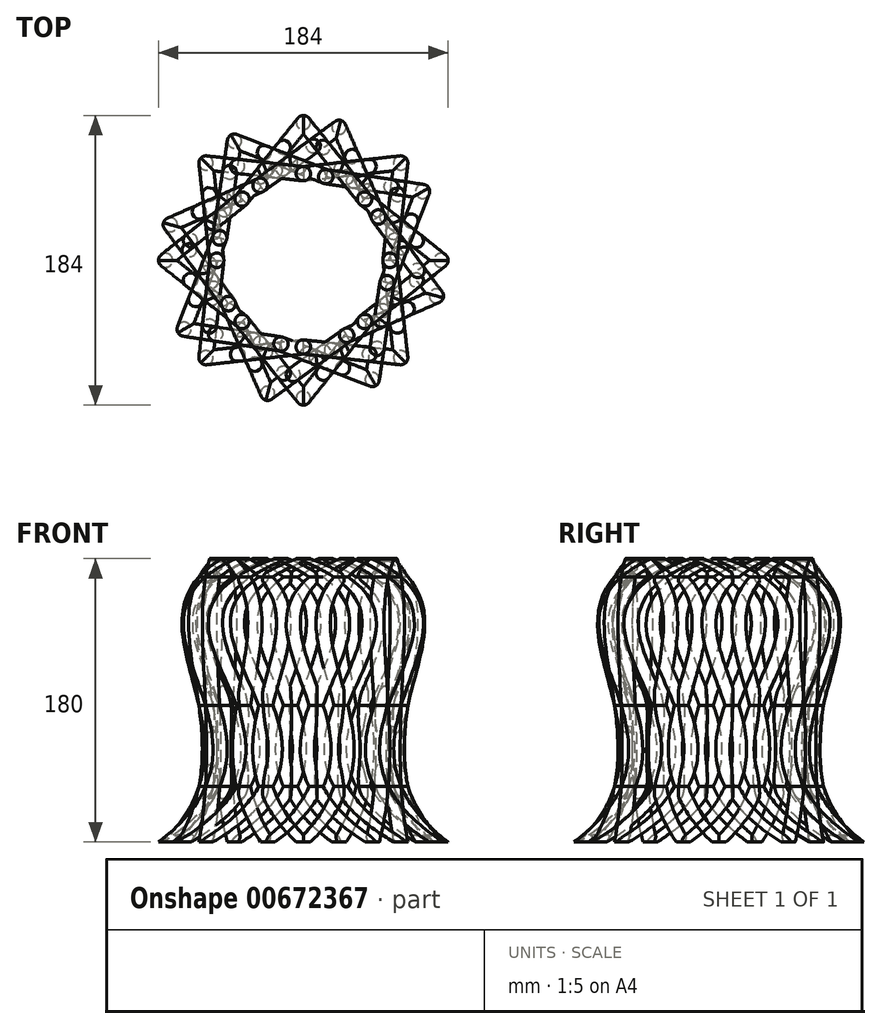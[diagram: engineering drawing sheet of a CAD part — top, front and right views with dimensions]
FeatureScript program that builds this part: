
annotation { "Feature Type Name" : "Feature", "Feature Type Description" : "" }
export const myFeature = defineFeature(function(context is Context, id is Id, definition is map)
    precondition{}
    {
        {
            var Q0;
            Q0=qCreatedBy(makeId("Top.planeOp"),FACE);
            var sketch = newSketch(context, id + "F0", { "sketchPlane" : qUnion([Q0])});
            skCircle(sketch, "E0", {"center": v(0, 0) * mm, "radius": 87.5 * mm});
            skSolve(sketch);
        }
        {
            var Q0;
            Q0=qCreatedBy(makeId("Top.planeOp"),FACE);
            cPlane(context, id + "F1", {"entities" : qUnion([Q0]), "cplaneType" : CPlaneType.OFFSET, "offset" : 180 * mm, "width" : 150 * mm, "height" : 150 * mm});
        }
        {
            var Q0;
            Q0=qCreatedBy(id+"F1.planeOp",FACE);
            var sketch = newSketch(context, id + "F2", { "sketchPlane" : qUnion([Q0])});
            skCircle(sketch, "E1", {"center": v(0, 0) * mm, "radius": 55 * mm});
            skSolve(sketch);
        }
        {
            var Q0;
            Q0=qCreatedBy(makeId("Top.planeOp"),FACE);
            var sketch = newSketch(context, id + "F3", { "sketchPlane" : qUnion([Q0])});
            skCircle(sketch, "E2.0", {"center": v(0, 0) * mm, "radius": 87.5 * mm, "construction": true});
            skCircle(sketch, "E3", {"center": v(-87.5, 0) * mm, "radius": 4.5 * mm});
            skSolve(sketch);
        }
        {
            var Q0;
            Q0=qCreatedBy(id+"F1.planeOp",FACE);
            var sketch = newSketch(context, id + "F4", { "sketchPlane" : qUnion([Q0])});
            skCircle(sketch, "E4.0.0", {"center": v(0, 0) * mm, "radius": 55 * mm, "construction": true});
            skCircle(sketch, "E5", {"center": v(-38.8, -38.98) * mm, "radius": 4.5 * mm});
            skSolve(sketch);
        }
        {
            var Q0;
            Q0=qCreatedBy(makeId("Top.planeOp"),FACE);
            var sketch = newSketch(context, id + "F5", { "sketchPlane" : qUnion([Q0])});
            skCircle(sketch, "E6.0", {"center": v(-87.5, 0) * mm, "radius": 4.5 * mm, "construction": true});
            skCircle(sketch, "E7.0", {"center": v(-38.8, -38.98) * mm, "radius": 4.5 * mm, "construction": true});
            skLineSegment(sketch, "E8", {"start": v(-87.5, 0) * mm, "end": v(-38.8, -38.98) * mm});
            skSolve(sketch);
        }
        {
            var Q0;
            Q0=sQuery(id+"F5.wireOp",EDGE,"E8");
            cPlane(context, id + "F6", {"entities" : qUnion([Q0]), "cplaneType" : CPlaneType.LINE_ANGLE, "offset" : 25 * mm, "angle" : 0 * degree, "width" : 150 * mm, "height" : 150 * mm});
        }
        {
            var Q0;
            Q0=qCreatedBy(id+"F6.planeOp",FACE);
            var sketch = newSketch(context, id + "F7", { "sketchPlane" : qUnion([Q0])});
            skPoint(sketch, "E9.0", {"position": v(68.31, 0) * mm});
            skPoint(sketch, "E10.0", {"position": v(5.94, 180) * mm});
            skFitSpline(sketch, "E11", {"points": [v(68.31, 0) * mm, v(5.94, 180) * mm], "startDerivative": vector(-358.3, 212.23) * mm, "endDerivative": vector(-348.03, 128.54) * mm});
            skSolve(sketch);
        }
        {
            var Q0;
            Q0=makeQuery(id+"F3.imprint","IMPRINT",FACE,{"disambiguationData":[TD([[makeQuery(id+"F3.imprint","IMPRINT",EDGE,{"derivedFrom":sQuery(id+"F3.wireOp",EDGE,"E3")}),1.0]])]});
            var Q1;
            Q1=sQuery(id+"F7.wireOp",EDGE,"E11");
            sweep(context, id + "F8", {"profiles" : qUnion([Q0]), "path" : qUnion([Q1]), "profileControl" : ProfileControlMode.KEEP_ORIENTATION});
        }
        {
            var Q0;
            Q0=qCreatedBy(makeId("Front.planeOp"),FACE);
            var sketch = newSketch(context, id + "F9", { "sketchPlane" : qUnion([Q0])});
            skLineSegment(sketch, "E12", {"start": v(0, 180.1) * mm, "end": v(0, -48.75) * mm});
            skSolve(sketch);
        }
        {
            var Q0;
            Q0=makeQuery(id+"F8.opSweep","SWEPT_BODY",BODY,{"disambiguationData":[OSD([sQuery(id+"F3.wireOp",EDGE,"E3"),sQuery(id+"F7.wireOp",EDGE,"E11")])]});
            var Q1;
            Q1=qCreatedBy(makeId("Right.planeOp"),FACE);
            mirror(context, id + "F10", {"entities" : qUnion([Q0]), "mirrorPlane" : qUnion([Q1])});
        }
        {
            var Q0;
            Q0=makeQuery(id+"F8.opSweep","SWEPT_BODY",BODY,{"disambiguationData":[OSD([sQuery(id+"F3.wireOp",EDGE,"E3"),sQuery(id+"F7.wireOp",EDGE,"E11")])]});
            var Q1;
            Q1=sQuery(id+"F9.wireOp",EDGE,"E12");
            circularPattern(context, id + "F11", {"operationType" : NewBodyOperationType.ADD, "entities" : qUnion([Q0]), "axis" : qUnion([Q1]), "angle" : 360 * degree, "instanceCount" : 8, "equalSpace" : true, "computeTransformsWithoutBuiltin" : true});
        }
        {
            var Q0;
            Q0=makeQuery(id+"F10.opPattern","COPY",BODY,{"derivedFrom":makeQuery(id+"F8.opSweep","SWEPT_BODY",BODY,{"disambiguationData":[OSD([sQuery(id+"F3.wireOp",EDGE,"E3"),sQuery(id+"F7.wireOp",EDGE,"E11")])]}),"instanceName":"1"});
            var Q1;
            Q1=sQuery(id+"F9.wireOp",EDGE,"E12");
            circularPattern(context, id + "F12", {"operationType" : NewBodyOperationType.ADD, "entities" : qUnion([Q0]), "axis" : qUnion([Q1]), "angle" : 360 * degree, "instanceCount" : 8, "equalSpace" : true, "computeTransformsWithoutBuiltin" : true});
        }
        {
            var Q0;
            Q0=makeQuery(id+"F11.opPattern","COPY",BODY,{"derivedFrom":makeQuery(id+"F8.opSweep","SWEPT_BODY",BODY,{"disambiguationData":[OSD([sQuery(id+"F3.wireOp",EDGE,"E3"),sQuery(id+"F7.wireOp",EDGE,"E11")])]}),"instanceName":"4"});
            var Q1;
            Q1=makeQuery(id+"F11.opPattern","COPY",BODY,{"derivedFrom":makeQuery(id+"F8.opSweep","SWEPT_BODY",BODY,{"disambiguationData":[OSD([sQuery(id+"F3.wireOp",EDGE,"E3"),sQuery(id+"F7.wireOp",EDGE,"E11")])]}),"instanceName":"5"});
            var Q2;
            Q2=makeQuery(id+"F11.opPattern","COPY",BODY,{"derivedFrom":makeQuery(id+"F8.opSweep","SWEPT_BODY",BODY,{"disambiguationData":[OSD([sQuery(id+"F3.wireOp",EDGE,"E3"),sQuery(id+"F7.wireOp",EDGE,"E11")])]}),"instanceName":"6"});
            var Q3;
            Q3=makeQuery(id+"F11.opPattern","COPY",BODY,{"derivedFrom":makeQuery(id+"F8.opSweep","SWEPT_BODY",BODY,{"disambiguationData":[OSD([sQuery(id+"F3.wireOp",EDGE,"E3"),sQuery(id+"F7.wireOp",EDGE,"E11")])]}),"instanceName":"7"});
            var Q4;
            Q4=makeQuery(id+"F12.opPattern","COPY",BODY,{"derivedFrom":makeQuery(id+"F10.opPattern","COPY",BODY,{"derivedFrom":makeQuery(id+"F8.opSweep","SWEPT_BODY",BODY,{"disambiguationData":[OSD([sQuery(id+"F3.wireOp",EDGE,"E3"),sQuery(id+"F7.wireOp",EDGE,"E11")])]}),"instanceName":"1"}),"instanceName":"2"});
            var Q5;
            Q5=makeQuery(id+"F12.opPattern","COPY",BODY,{"derivedFrom":makeQuery(id+"F10.opPattern","COPY",BODY,{"derivedFrom":makeQuery(id+"F8.opSweep","SWEPT_BODY",BODY,{"disambiguationData":[OSD([sQuery(id+"F3.wireOp",EDGE,"E3"),sQuery(id+"F7.wireOp",EDGE,"E11")])]}),"instanceName":"1"}),"instanceName":"1"});
            var Q6;
            Q6=makeQuery(id+"F10.opPattern","COPY",BODY,{"derivedFrom":makeQuery(id+"F8.opSweep","SWEPT_BODY",BODY,{"disambiguationData":[OSD([sQuery(id+"F3.wireOp",EDGE,"E3"),sQuery(id+"F7.wireOp",EDGE,"E11")])]}),"instanceName":"1"});
            var Q7;
            Q7=makeQuery(id+"F8.opSweep","SWEPT_BODY",BODY,{"disambiguationData":[OSD([sQuery(id+"F3.wireOp",EDGE,"E3"),sQuery(id+"F7.wireOp",EDGE,"E11")])]});
            var Q8;
            Q8=makeQuery(id+"F12.opPattern","COPY",BODY,{"derivedFrom":makeQuery(id+"F10.opPattern","COPY",BODY,{"derivedFrom":makeQuery(id+"F8.opSweep","SWEPT_BODY",BODY,{"disambiguationData":[OSD([sQuery(id+"F3.wireOp",EDGE,"E3"),sQuery(id+"F7.wireOp",EDGE,"E11")])]}),"instanceName":"1"}),"instanceName":"3"});
            var Q9;
            Q9=makeQuery(id+"F12.opPattern","COPY",BODY,{"derivedFrom":makeQuery(id+"F10.opPattern","COPY",BODY,{"derivedFrom":makeQuery(id+"F8.opSweep","SWEPT_BODY",BODY,{"disambiguationData":[OSD([sQuery(id+"F3.wireOp",EDGE,"E3"),sQuery(id+"F7.wireOp",EDGE,"E11")])]}),"instanceName":"1"}),"instanceName":"4"});
            var Q10;
            Q10=makeQuery(id+"F12.opPattern","COPY",BODY,{"derivedFrom":makeQuery(id+"F10.opPattern","COPY",BODY,{"derivedFrom":makeQuery(id+"F8.opSweep","SWEPT_BODY",BODY,{"disambiguationData":[OSD([sQuery(id+"F3.wireOp",EDGE,"E3"),sQuery(id+"F7.wireOp",EDGE,"E11")])]}),"instanceName":"1"}),"instanceName":"5"});
            var Q11;
            Q11=makeQuery(id+"F11.opPattern","COPY",BODY,{"derivedFrom":makeQuery(id+"F8.opSweep","SWEPT_BODY",BODY,{"disambiguationData":[OSD([sQuery(id+"F3.wireOp",EDGE,"E3"),sQuery(id+"F7.wireOp",EDGE,"E11")])]}),"instanceName":"2"});
            var Q12;
            Q12=makeQuery(id+"F12.opPattern","COPY",BODY,{"derivedFrom":makeQuery(id+"F10.opPattern","COPY",BODY,{"derivedFrom":makeQuery(id+"F8.opSweep","SWEPT_BODY",BODY,{"disambiguationData":[OSD([sQuery(id+"F3.wireOp",EDGE,"E3"),sQuery(id+"F7.wireOp",EDGE,"E11")])]}),"instanceName":"1"}),"instanceName":"6"});
            var Q13;
            Q13=makeQuery(id+"F11.opPattern","COPY",BODY,{"derivedFrom":makeQuery(id+"F8.opSweep","SWEPT_BODY",BODY,{"disambiguationData":[OSD([sQuery(id+"F3.wireOp",EDGE,"E3"),sQuery(id+"F7.wireOp",EDGE,"E11")])]}),"instanceName":"3"});
            var Q14;
            Q14=makeQuery(id+"F12.opPattern","COPY",BODY,{"derivedFrom":makeQuery(id+"F10.opPattern","COPY",BODY,{"derivedFrom":makeQuery(id+"F8.opSweep","SWEPT_BODY",BODY,{"disambiguationData":[OSD([sQuery(id+"F3.wireOp",EDGE,"E3"),sQuery(id+"F7.wireOp",EDGE,"E11")])]}),"instanceName":"1"}),"instanceName":"7"});
            var Q15;
            Q15=sQuery(id+"F9.wireOp",EDGE,"E12");
            circularPattern(context, id + "F13", {"entities" : qUnion([Q0, Q1, Q2, Q3, Q4, Q5, Q6, Q7, Q8, Q9, Q10, Q11, Q12, Q13, Q14]), "axis" : qUnion([Q15]), "angle" : 15 * degree, "instanceCount" : 2, "equalSpace" : true, "computeTransformsWithoutBuiltin" : true});
        }
    });
